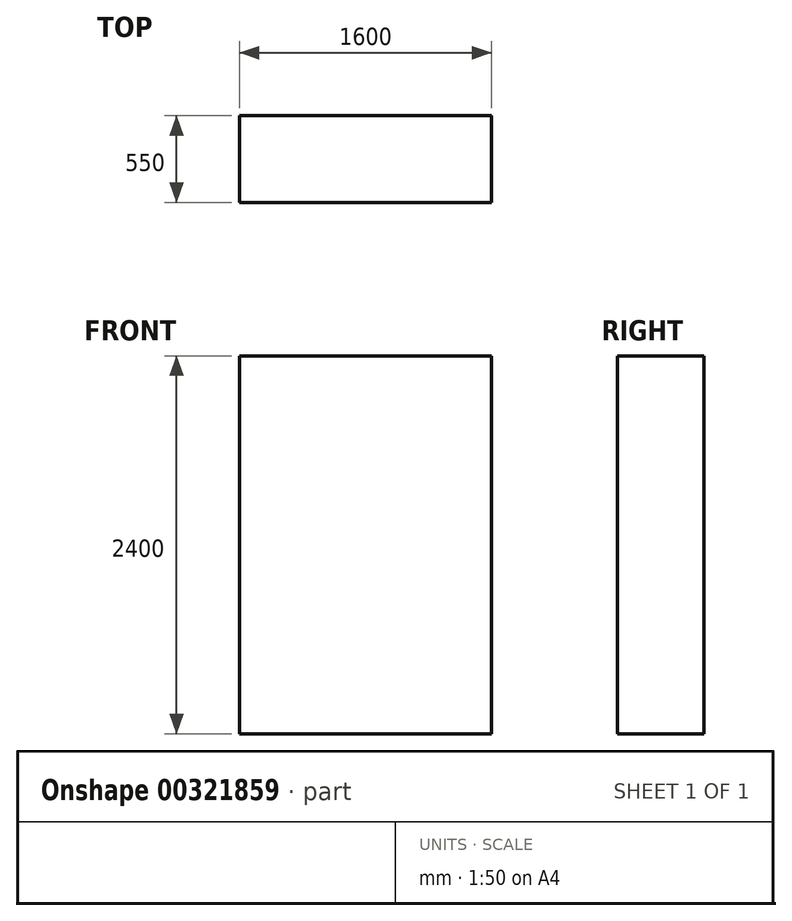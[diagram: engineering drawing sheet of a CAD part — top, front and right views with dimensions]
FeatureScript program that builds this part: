
annotation { "Feature Type Name" : "Feature", "Feature Type Description" : "" }
export const myFeature = defineFeature(function(context is Context, id is Id, definition is map)
    precondition{}
    {
        {
            var Q0;
            Q0=qCreatedBy(makeId("Top.planeOp"),FACE);
            var sketch = newSketch(context, id + "F0", { "sketchPlane" : qUnion([Q0])});
            skLineSegment(sketch, "E0.bottom", {"start": v(800, 275) * mm, "end": v(-800, 275) * mm});
            skLineSegment(sketch, "E0.top", {"start": v(800, -275) * mm, "end": v(-800, -275) * mm});
            skLineSegment(sketch, "E0.left", {"start": v(800, 275) * mm, "end": v(800, -275) * mm});
            skLineSegment(sketch, "E0.right", {"start": v(-800, 275) * mm, "end": v(-800, -275) * mm});
            skPoint(sketch, "E0.middle", {"position": v(0, 0) * mm});
            skSolve(sketch);
        }
        {
            var Q0;
            Q0=makeQuery(id+"F0.imprint","IMPRINT",FACE,{"disambiguationData":[TD([[makeQuery(id+"F0.imprint","IMPRINT",EDGE,{"derivedFrom":sQuery(id+"F0.wireOp",EDGE,"E0.bottom")}),1.0]])]});
            extrude(context, id + "F1", {"entities" : qUnion([Q0]), "depth" : 2400 * mm});
        }
    });
